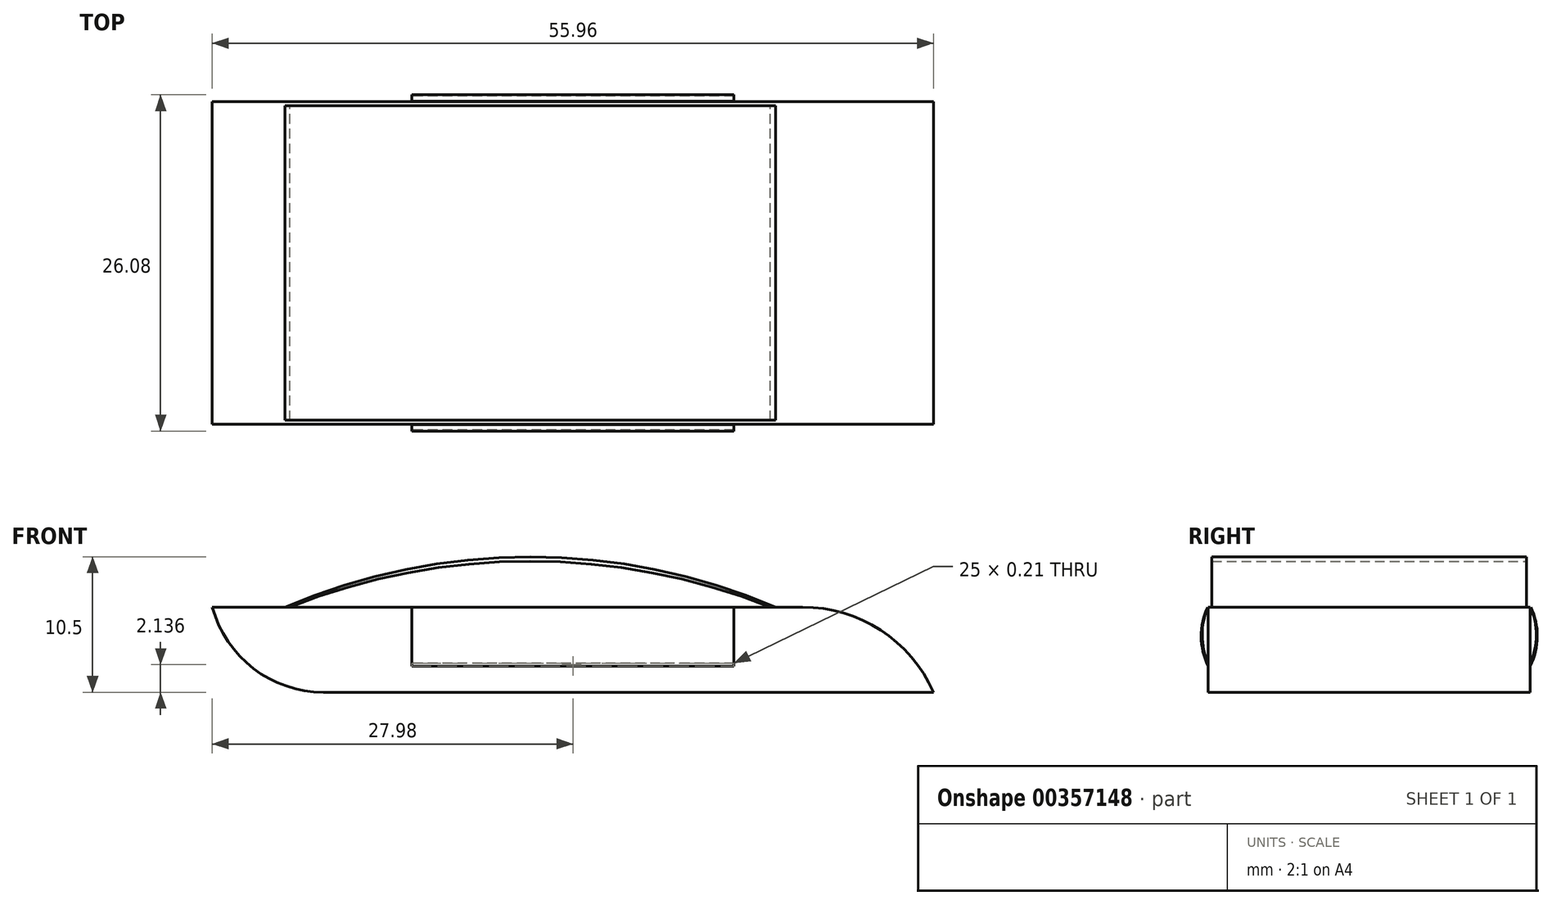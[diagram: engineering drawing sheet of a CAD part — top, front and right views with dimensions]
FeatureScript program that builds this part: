
annotation { "Feature Type Name" : "Feature", "Feature Type Description" : "" }
export const myFeature = defineFeature(function(context is Context, id is Id, definition is map)
    precondition{}
    {
        {
            var Q0;
            Q0=qCreatedBy(makeId("Top.planeOp"),FACE);
            var sketch = newSketch(context, id + "F0", { "sketchPlane" : qUnion([Q0])});
            skLineSegment(sketch, "E0.bottom", {"start": v(-27.98, -12.5) * mm, "end": v(27.98, -12.5) * mm});
            skLineSegment(sketch, "E0.top", {"start": v(-27.98, 12.5) * mm, "end": v(27.98, 12.5) * mm});
            skLineSegment(sketch, "E0.left", {"start": v(-27.98, -12.5) * mm, "end": v(-27.98, 12.5) * mm});
            skLineSegment(sketch, "E0.right", {"start": v(27.98, -12.5) * mm, "end": v(27.98, 12.5) * mm});
            skPoint(sketch, "E0.middle", {"position": v(0, 0) * mm});
            skSolve(sketch);
        }
        {
            var Q0;
            Q0 = qSketchRegion(id + "F0", true);
            extrude(context, id + "F1", {"entities" : qUnion([Q0]), "depth" : 6.6 * mm});
        }
        {
            var Q0;
            Q0=qCreatedBy(makeId("Front.planeOp"),FACE);
            var sketch = newSketch(context, id + "F2", { "sketchPlane" : qUnion([Q0])});
            skArc(sketch, "E1", {"start": v(22.11, 3.3) * mm, "mid": v(-2.74, 10.15) * mm, "end": v(-27.74, 3.88) * mm});
            skArc(sketch, "E2", {"start": v(22.11, 3.3) * mm, "mid": v(-2.73, 10.5) * mm, "end": v(-27.74, 3.88) * mm});
            skSolve(sketch);
        }
        {
            var Q0;
            Q0 = qSketchRegion(id + "F2", true);
            extrude(context, id + "F3", {"entities" : qUnion([Q0]), "operationType" : NewBodyOperationType.ADD, "endBound" : BoundingType.SYMMETRIC, "depth" : 24.4 * mm});
        }
        {
            var Q0;
            Q0=makeQuery(id+"F1.opExtrude","CAP_EDGE",EDGE,{"disambiguationData":[OSD([sQuery(id+"F0.wireOp",EDGE,"E0.right")])],"isStart":false});
            fillet(context, id + "F4", {"entities" : qUnion([Q0]), "radius" : 11.1 * mm, "tangentPropagation" : true, "allowEdgeOverflow" : false});
        }
        {
            var Q0;
            Q0=makeQuery(id+"F1.opExtrude","CAP_EDGE",EDGE,{"disambiguationData":[OSD([sQuery(id+"F0.wireOp",EDGE,"E0.left")])],"isStart":true});
            fillet(context, id + "F5", {"entities" : qUnion([Q0]), "radius" : 8.93 * mm, "tangentPropagation" : true, "allowEdgeOverflow" : false});
        }
        {
            var Q0;
            Q0=qCreatedBy(makeId("Right.planeOp"),FACE);
            var sketch = newSketch(context, id + "F6", { "sketchPlane" : qUnion([Q0])});
            skArc(sketch, "E3", {"start": v(-12.53, 6.6) * mm, "mid": v(-12.76, 2.99) * mm, "end": v(-10.73, 0) * mm});
            skArc(sketch, "E4", {"start": v(-12.53, 6.6) * mm, "mid": v(-12.85, 2.96) * mm, "end": v(-10.73, 0) * mm});
            skArc(sketch, "E5.MirrorCS", {"start": v(12.53, 6.6) * mm, "mid": v(12.76, 2.99) * mm, "end": v(10.73, 0) * mm});
            skArc(sketch, "E6.MirrorCS", {"start": v(12.53, 6.6) * mm, "mid": v(12.85, 2.96) * mm, "end": v(10.73, 0) * mm});
            skSolve(sketch);
        }
        {
            var Q0;
            Q0 = qSketchRegion(id + "F6", true);
            extrude(context, id + "F7", {"entities" : qUnion([Q0]), "operationType" : NewBodyOperationType.ADD, "endBound" : BoundingType.SYMMETRIC, "depth" : 25 * mm});
        }
    });
